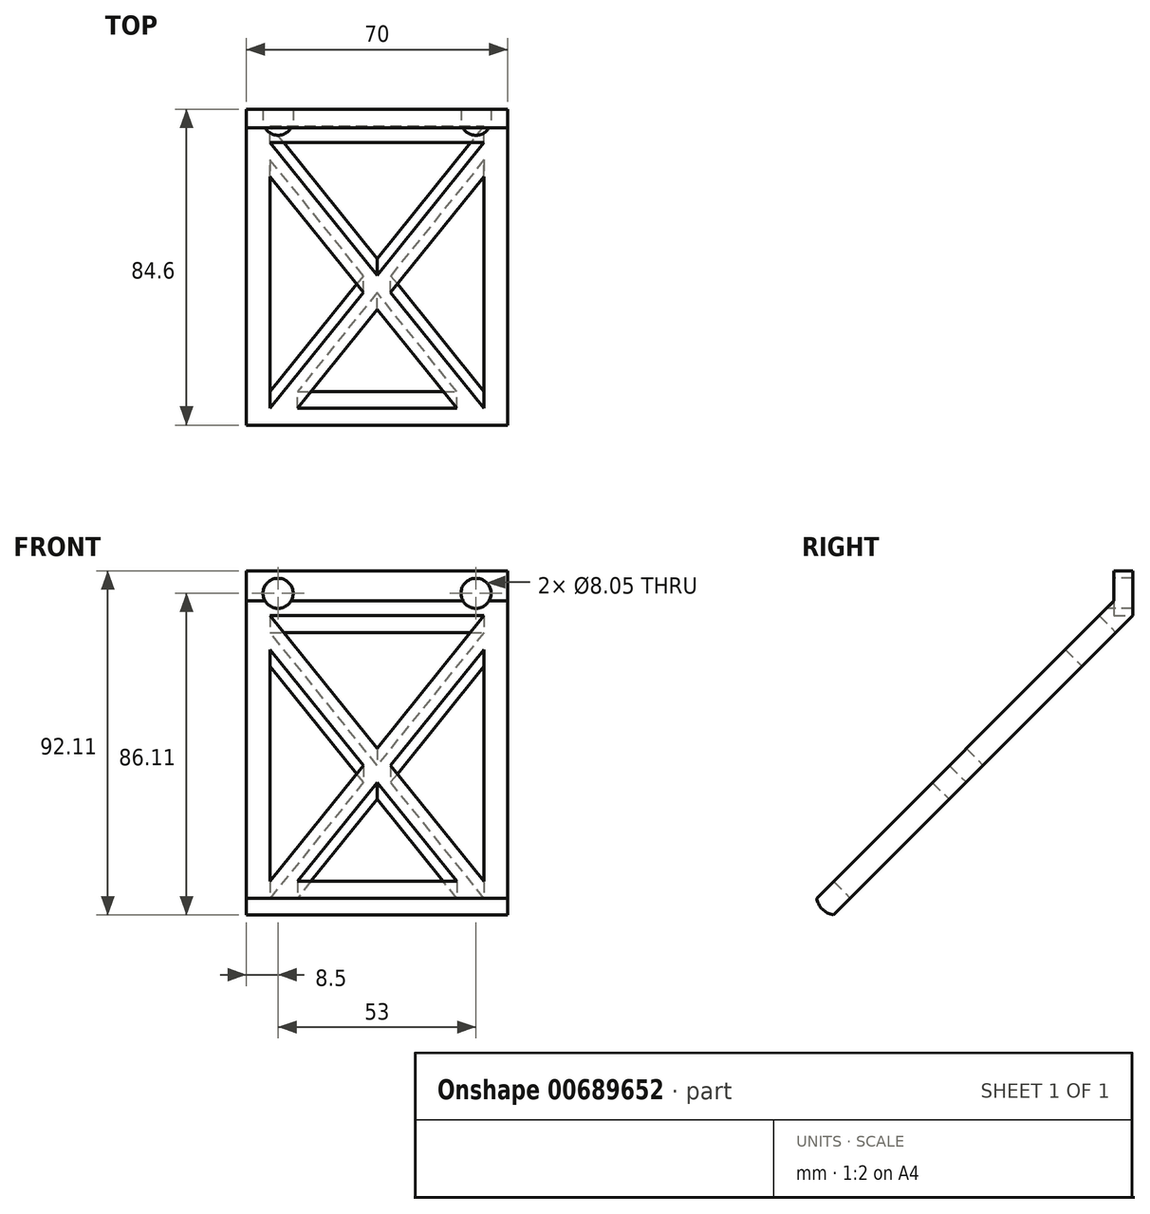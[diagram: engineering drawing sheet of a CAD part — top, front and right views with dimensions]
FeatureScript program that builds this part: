
annotation { "Feature Type Name" : "Feature", "Feature Type Description" : "" }
export const myFeature = defineFeature(function(context is Context, id is Id, definition is map)
    precondition{}
    {
        {
            var Q0;
            Q0=qCreatedBy(makeId("Front.planeOp"),FACE);
            var sketch = newSketch(context, id + "F0", { "sketchPlane" : qUnion([Q0])});
            skLineSegment(sketch, "E0.bottom", {"start": v(-35, 6) * mm, "end": v(35, 6) * mm});
            skLineSegment(sketch, "E0.top", {"start": v(-35, -6) * mm, "end": v(35, -6) * mm});
            skLineSegment(sketch, "E0.left", {"start": v(-35, 6) * mm, "end": v(-35, -6) * mm});
            skLineSegment(sketch, "E0.right", {"start": v(35, 6) * mm, "end": v(35, -6) * mm});
            skPoint(sketch, "E0.middle", {"position": v(0, 0) * mm});
            skSolve(sketch);
        }
        {
            var Q0;
            Q0 = qSketchRegion(id + "F0", true);
            extrude(context, id + "F1", {"entities" : qUnion([Q0]), "depth" : 5 * mm, "offsetDistance" : 25.4 * mm});
        }
        {
            var Q0;
            Q0=makeQuery(id+"F1.opExtrude","CAP_FACE",FACE,{"disambiguationData":[OSD([sQuery(id+"F0.wireOp",EDGE,"E0.bottom"),sQuery(id+"F0.wireOp",EDGE,"E0.top"),sQuery(id+"F0.wireOp",EDGE,"E0.left"),sQuery(id+"F0.wireOp",EDGE,"E0.right")])],"isStart":false});
            var sketch = newSketch(context, id + "F2", { "sketchPlane" : qUnion([Q0])});
            skCircle(sketch, "E1", {"center": v(-26.5, 0) * mm, "radius": 4.03 * mm});
            skCircle(sketch, "E2.MirrorC", {"center": v(26.5, 0) * mm, "radius": 4.03 * mm});
            skSolve(sketch);
        }
        {
            var Q0;
            Q0 = qSketchRegion(id + "F2", true);
            extrude(context, id + "F3", {"entities" : qUnion([Q0]), "operationType" : NewBodyOperationType.REMOVE, "oppositeDirection" : true, "depth" : 25.4 * mm, "offsetDistance" : 25.4 * mm});
        }
        {
            var Q0;
            Q0=makeQuery(id+"F1.opExtrude","SWEPT_FACE",FACE,{"disambiguationData":[OSD([sQuery(id+"F0.wireOp",EDGE,"E0.right")])]});
            var sketch = newSketch(context, id + "F4", { "sketchPlane" : qUnion([Q0])});
            skLineSegment(sketch, "E3", {"start": v(0, -6) * mm, "end": v(-80.1, -86.1) * mm});
            skLineSegment(sketch, "E4.0", {"start": v(-5, -2.02) * mm, "end": v(-84.6, -81.62) * mm});
            skLineSegment(sketch, "E5", {"start": v(0, -6) * mm, "end": v(-5, -6) * mm});
            skLineSegment(sketch, "E6", {"start": v(-5, -6) * mm, "end": v(-5, -2.02) * mm});
            skArc(sketch, "E7", {"start": v(-84.6, -81.62) * mm, "mid": v(-83.07, -84.58) * mm, "end": v(-80.1, -86.1) * mm});
            skSolve(sketch);
        }
        {
            var Q0;
            Q0 = qSketchRegion(id + "F4", true);
            extrude(context, id + "F5", {"entities" : qUnion([Q0]), "operationType" : NewBodyOperationType.ADD, "oppositeDirection" : true, "depth" : 69.98 * mm, "offsetDistance" : 25.4 * mm});
        }
        {
            var Q0;
            Q0=makeQuery(id+"F1.opExtrude","CAP_FACE",FACE,{"disambiguationData":[OSD([sQuery(id+"F0.wireOp",EDGE,"E0.bottom"),sQuery(id+"F0.wireOp",EDGE,"E0.top"),sQuery(id+"F0.wireOp",EDGE,"E0.left"),sQuery(id+"F0.wireOp",EDGE,"E0.right")])],"isStart":true});
            var sketch = newSketch(context, id + "F6", { "sketchPlane" : qUnion([Q0])});
            skCircle(sketch, "E8.0", {"center": v(26.5, 0) * mm, "radius": 4.03 * mm});
            skCircle(sketch, "E9.0", {"center": v(-26.5, 0) * mm, "radius": 4.03 * mm});
            skSolve(sketch);
        }
        {
            var Q0;
            Q0 = qSketchRegion(id + "F6", true);
            extrude(context, id + "F7", {"entities" : qUnion([Q0]), "operationType" : NewBodyOperationType.REMOVE, "oppositeDirection" : true, "depth" : 25.4 * mm, "offsetDistance" : 25.4 * mm});
        }
        {
            var Q0;
            Q0=makeQuery(id+"F5.opExtrude","SWEPT_FACE",FACE,{"disambiguationData":[OSD([sQuery(id+"F4.wireOp",EDGE,"E3")])]});
            var sketch = newSketch(context, id + "F8", { "sketchPlane" : qUnion([Q0])});
            skLineSegment(sketch, "E10.0", {"start": v(-28.65, -23.43) * mm, "end": v(-28.65, -111.18) * mm});
            skLineSegment(sketch, "E10.1", {"start": v(28.63, -10.6) * mm, "end": v(-28.65, -10.6) * mm});
            skLineSegment(sketch, "E10.2", {"start": v(28.63, -23.43) * mm, "end": v(28.63, -111.18) * mm});
            skLineSegment(sketch, "E10.3", {"start": v(21.32, -111.18) * mm, "end": v(-21.34, -111.18) * mm});
            skLineSegment(sketch, "E11", {"start": v(-28.65, -10.6) * mm, "end": v(-0.01, -60.89) * mm});
            skLineSegment(sketch, "E12", {"start": v(-28.65, -111.18) * mm, "end": v(-3.67, -67.3) * mm});
            skLineSegment(sketch, "E13.0", {"start": v(-21.34, -111.18) * mm, "end": v(-0.01, -73.72) * mm});
            skLineSegment(sketch, "E14.0", {"start": v(-28.65, -23.43) * mm, "end": v(-3.67, -67.3) * mm});
            skLineSegment(sketch, "E15.trimOffspring", {"start": v(-0.01, -73.72) * mm, "end": v(21.32, -111.18) * mm});
            skLineSegment(sketch, "E16.trimOffspring", {"start": v(-0.01, -60.89) * mm, "end": v(28.63, -10.6) * mm});
            skLineSegment(sketch, "E17.trimOffspring", {"start": v(3.64, -67.3) * mm, "end": v(28.63, -111.18) * mm});
            skLineSegment(sketch, "E18.trimOffspring", {"start": v(3.64, -67.3) * mm, "end": v(28.63, -23.43) * mm});
            skSolve(sketch);
        }
        {
            var Q0;
            Q0 = qSketchRegion(id + "F8", true);
            extrude(context, id + "F9", {"entities" : qUnion([Q0]), "operationType" : NewBodyOperationType.REMOVE, "oppositeDirection" : true, "depth" : 25.4 * mm, "offsetDistance" : 25.4 * mm});
        }
    });
